# Revit family: Facade_60_Curtain_Wall_S22_Standard
name_source: partatom
category: Windows
revit_build: Autodesk Revit 2014 (Build: 20130308_1515(x64)
units: mm (PartAtom-declared; Revit-internal decimal feet)

## types (32) — shared parameters
DG Gasket Thickness = 12 mm  [stored 0.0393701 ft]
Description = Curtain wall, S22
Frame Bottom Gap = 30 mm  [stored 0.0984252 ft]
Frame Thickness = 102 mm
Glazing Bottom Gap = 70 mm
Glazing Side Gap = 40 mm  [stored 0.131234 ft]
Glazing Top Gap = 40 mm  [stored 0.131234 ft]
Half Expansion Break = No
Jamb Width = 60 mm  [stored 0.19685 ft]
Limit Door Height Max = 12129 mm
Limit Door Height Min = 729 mm
Limit Door Width Max = 6099 mm
Limit Door Width Min = 699 mm
Limit Panel Height Max = 6000 mm  [stored 19.685 ft]
Limit Panel Height Min = 300 mm  [stored 0.984252 ft]
Limit Panel Width Max = 3000 mm  [stored 9.84252 ft]
Limit Panel Width Min = 300 mm  [stored 0.984252 ft]
Manufacturer = Crealco
Max System DG Unit Thickness = 25 mm  [stored 0.082021 ft]
Model = Façade 60
Quarter Expansion Break = No
Sill Height = 85 mm  [stored 0.278871 ft]
Thermal Break Material = Plastic, Opaque Black
Top Profile Overhang = 6 mm  [stored 0.019685 ft]
URL = http://www.crealco.co.za
Wall Closure = By host
zero-valued in all types: Custom Offset From Exterior, Default Sill Height

## per-type parameters (varying)
| type | Custom Curtain Wall Height | Custom Curtain Wall Width | Custom Windload | Intruderprufe Insulated LowE SHGC Value | Intruderprufe Insulated LowE U Value | Intruderprufe Insulated SHGC Value | Intruderprufe Insulated U Value | Intruderprufe LowE SHGC Value | Intruderprufe LowE U Value | Intruderprufe SHGC Value | Intruderprufe U Value |
| F60-S22-1825-1000Pa | 2490 mm | 1790 mm  [stored 5.8727 ft] | 1000 mm  [stored 3.28084 ft] | 0.528 | 2.52 | 0.586 | 3.14 | 0.596 | 4.259 | 0.68 | 5.65 |
| F60-S22-1825-1500Pa | 2490 mm | 1790 mm  [stored 5.8727 ft] | 1500 mm  [stored 4.92126 ft] | 0.528 | 2.52 | 0.586 | 3.14 | 0.596 | 4.259 | 0.68 | 5.65 |
| F60-S22-1825-2000Pa | 2490 mm | 1790 mm  [stored 5.8727 ft] | 2000 mm  [stored 6.56168 ft] | 0.528 | 2.52 | 0.586 | 3.14 | 0.596 | 4.259 | 0.68 | 5.65 |
| F60-S22-2425-1000Pa | 2490 mm | 2390 mm  [stored 7.84121 ft] | 1000 mm  [stored 3.28084 ft] | 0.534 | 2.49 | 0.592 | 3.11 | 0.603 | 4.26 | 0.688 | 5.67 |
| F60-S22-2425-1500Pa | 2490 mm | 2390 mm  [stored 7.84121 ft] | 1500 mm  [stored 4.92126 ft] | 0.534 | 2.49 | 0.592 | 3.11 | 0.603 | 4.26 | 0.688 | 5.67 |
| F60-S22-2425-2000Pa | 2490 mm | 2390 mm  [stored 7.84121 ft] | 2000 mm  [stored 6.56168 ft] | 0.534 | 2.49 | 0.592 | 3.11 | 0.603 | 4.26 | 0.688 | 5.67 |
| F60-S22-3025-1000Pa | 2490 mm | 2990 mm | 1000 mm  [stored 3.28084 ft] | 0.542 | 2.44 | 0.601 | 3.08 | 0.612 | 4.22 | 0.698 | 5.69 |
| F60-S22-3025-1500Pa | 2490 mm | 2990 mm | 1500 mm  [stored 4.92126 ft] | 0.542 | 2.44 | 0.601 | 3.08 | 0.612 | 4.22 | 0.698 | 5.69 |
| F60-S22-3025-2000Pa | 2490 mm | 2990 mm | 2000 mm  [stored 6.56168 ft] | 0.542 | 2.44 | 0.601 | 3.08 | 0.612 | 4.22 | 0.698 | 5.69 |
| F60-S22-3625-1000Pa | 2490 mm | 3590 mm | 1000 mm  [stored 3.28084 ft] | 0.547 | 2.41 | 0.607 | 3.06 | 0.618 | 4.19 | 0.705 | 5.71 |
| F60-S22-3625-1500Pa | 2490 mm | 3590 mm | 1500 mm  [stored 4.92126 ft] | 0.547 | 2.41 | 0.607 | 3.06 | 0.618 | 4.19 | 0.705 | 5.71 |
| F60-S22-3625-2000Pa | 2490 mm | 3590 mm | 2000 mm  [stored 6.56168 ft] | 0.547 | 2.41 | 0.607 | 3.06 | 0.618 | 4.19 | 0.705 | 5.71 |
| F60-S22-4225-1000Pa | 2490 mm | 4190 mm  [stored 13.7467 ft] | 1000 mm  [stored 3.28084 ft] | 0.551 | 2.38 | 0.611 | 3.04 | 0.622 | 4.18 | 0.71 | 5.72 |
| F60-S22-4225-1500Pa | 2490 mm | 4190 mm  [stored 13.7467 ft] | 1500 mm  [stored 4.92126 ft] | 0.551 | 2.38 | 0.611 | 3.04 | 0.622 | 4.18 | 0.71 | 5.72 |
| F60-S22-4225-2000Pa | 2490 mm | 4190 mm  [stored 13.7467 ft] | 2000 mm  [stored 6.56168 ft] | 0.551 | 2.38 | 0.611 | 3.04 | 0.622 | 4.18 | 0.71 | 5.72 |
| F60-S22-4825-1000Pa | 2490 mm | 4790 mm  [stored 15.7152 ft] | 1000 mm  [stored 3.28084 ft] | 0.554 | 2.36 | 0.615 | 3.03 | 0.626 | 4.16 | 0.714 | 5.72 |
| F60-S22-4825-1500Pa | 2490 mm | 4790 mm  [stored 15.7152 ft] | 1500 mm  [stored 4.92126 ft] | 0.554 | 2.36 | 0.615 | 3.03 | 0.626 | 4.16 | 0.714 | 5.72 |
| F60-S22-4825-2000Pa | 2490 mm | 4790 mm  [stored 15.7152 ft] | 2000 mm  [stored 6.56168 ft] | 0.554 | 2.36 | 0.615 | 3.03 | 0.626 | 4.16 | 0.714 | 5.72 |
| F60-S22-5425-1000Pa | 2490 mm | 5390 mm  [stored 17.6837 ft] | 1000 mm  [stored 3.28084 ft] | 0.556 | 2.35 | 0.617 | 3.02 | 0.628 | 4.15 | 0.717 | 5.73 |
| F60-S22-5425-1500Pa | 2490 mm | 5390 mm  [stored 17.6837 ft] | 1500 mm  [stored 4.92126 ft] | 0.556 | 2.35 | 0.617 | 3.02 | 0.628 | 4.15 | 0.717 | 5.73 |
| F60-S22-5425-2000Pa | 2490 mm | 5390 mm  [stored 17.6837 ft] | 2000 mm  [stored 6.56168 ft] | 0.556 | 2.35 | 0.617 | 3.02 | 0.628 | 4.15 | 0.717 | 5.73 |
| F60-S22-6025-1000Pa | 2490 mm | 5990 mm  [stored 19.6522 ft] | 1000 mm  [stored 3.28084 ft] | 0.558 | 2.34 | 0.619 | 3.01 | 0.63 | 4.14 | 0.72 | 5.74 |
| F60-S22-6025-1500Pa | 2490 mm | 5990 mm  [stored 19.6522 ft] | 1500 mm  [stored 4.92126 ft] | 0.558 | 2.34 | 0.619 | 3.01 | 0.63 | 4.14 | 0.72 | 5.74 |
| F60-S22-6025-2000Pa | 2490 mm | 5990 mm  [stored 19.6522 ft] | 2000 mm  [stored 6.56168 ft] | 0.558 | 2.34 | 0.619 | 3.01 | 0.63 | 4.14 | 0.72 | 5.74 |
| F60-S22-1850-1000Pa | 4990 mm  [stored 16.3714 ft] | 1790 mm  [stored 5.8727 ft] | 1000 mm  [stored 3.28084 ft] | 0.55 | 2.37 | 0.611 | 3.02 | 0.622 | 4.1 | 0.71 | 5.62 |
| F60-S22-1850-1500Pa | 4990 mm  [stored 16.3714 ft] | 1790 mm  [stored 5.8727 ft] | 1500 mm  [stored 4.92126 ft] | 0.55 | 2.37 | 0.611 | 3.02 | 0.622 | 4.1 | 0.71 | 5.62 |
| F60-S22-1850-2000Pa | 4990 mm  [stored 16.3714 ft] | 1790 mm  [stored 5.8727 ft] | 2000 mm  [stored 6.56168 ft] | 0.55 | 2.37 | 0.611 | 3.02 | 0.622 | 4.1 | 0.71 | 5.62 |
| F60-S22-2450-1000Pa | 4990 mm  [stored 16.3714 ft] | 2390 mm  [stored 7.84121 ft] | 1000 mm  [stored 3.28084 ft] | 0.556 | 2.33 | 0.617 | 2.99 | 0.629 | 4.07 | 0.718 | 5.64 |
| F60-S22-2450-1500Pa | 4990 mm  [stored 16.3714 ft] | 2390 mm  [stored 7.84121 ft] | 1500 mm  [stored 4.92126 ft] | 0.556 | 2.33 | 0.617 | 2.99 | 0.629 | 4.07 | 0.718 | 5.64 |
| F60-S22-3050-1000Pa | 4990 mm  [stored 16.3714 ft] | 2990 mm | 1000 mm  [stored 3.28084 ft] | 0.565 | 2.27 | 0.627 | 2.95 | 0.638 | 4.03 | 0.729 | 5.67 |
| F60-S22-3650-1000Pa | 4990 mm  [stored 16.3714 ft] | 3590 mm | 1000 mm  [stored 3.28084 ft] | 0.57 | 2.24 | 0.633 | 2.93 | 0.645 | 4 | 0.736 | 5.68 |
| F60-S22-4250-1000Pa | 4990 mm  [stored 16.3714 ft] | 4190 mm  [stored 13.7467 ft] | 1000 mm  [stored 3.28084 ft] | 0.574 | 2.21 | 0.637 | 2.91 | 0.649 | 3.97 | 0.742 | 5.69 |

note: [stored X ft] marks values corroborated as IEEE doubles in the binary element streams (Revit-internal decimal feet)

## geometry (parser evidence)
native form markers: Sweep x19
no freeform markers — native parametric forms only
